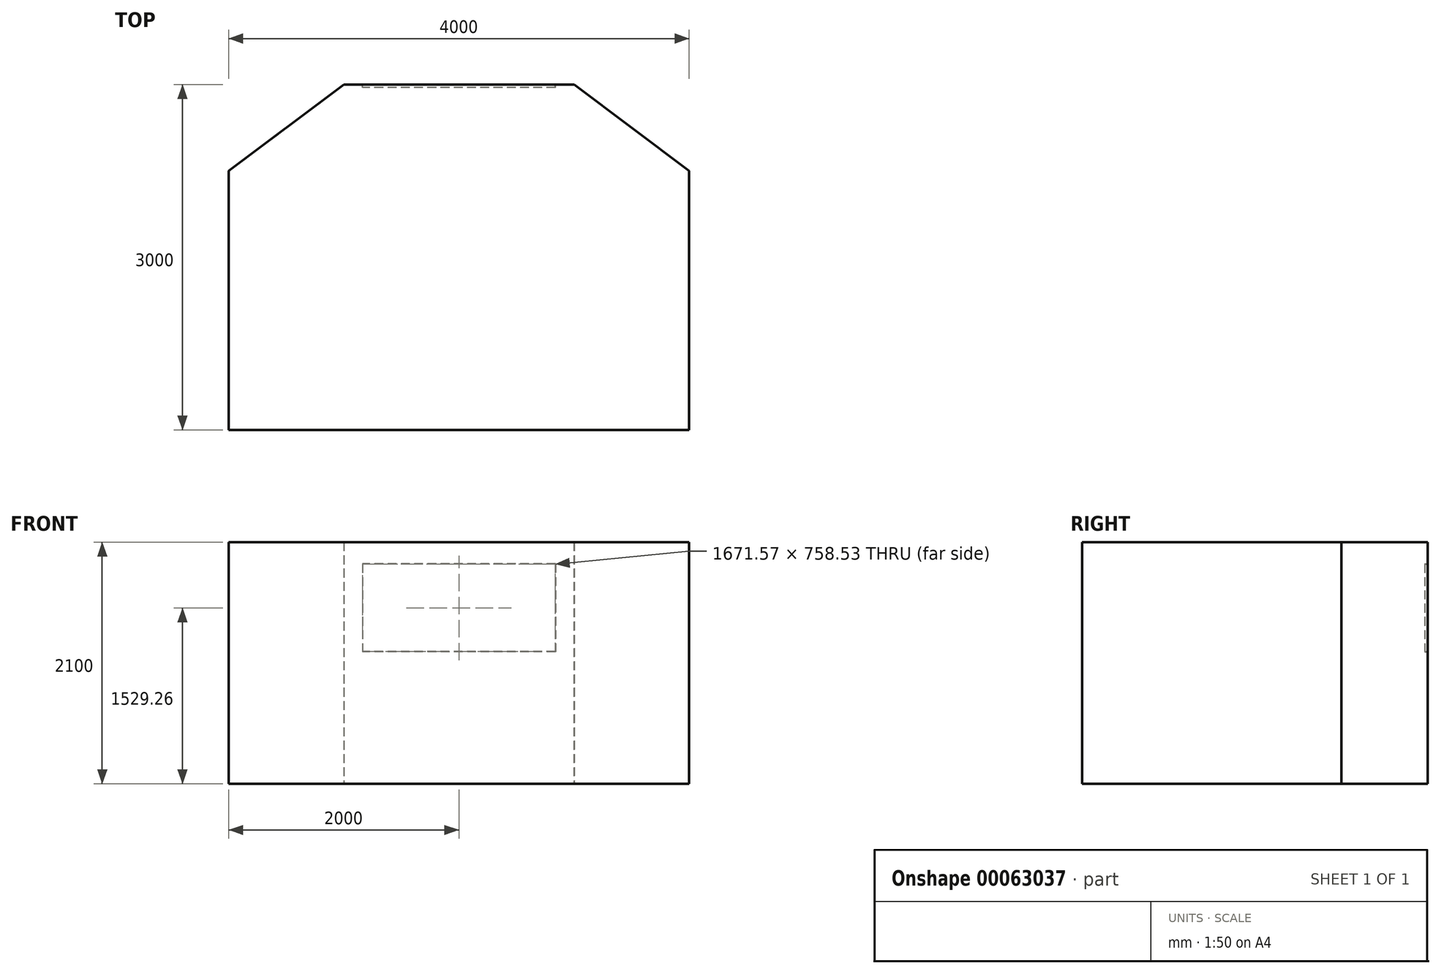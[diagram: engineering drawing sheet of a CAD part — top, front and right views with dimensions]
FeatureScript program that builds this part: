
annotation { "Feature Type Name" : "Feature", "Feature Type Description" : "" }
export const myFeature = defineFeature(function(context is Context, id is Id, definition is map)
    precondition{}
    {
        {
            var Q0;
            Q0=qCreatedBy(makeId("Top.planeOp"),FACE);
            var sketch = newSketch(context, id + "F0", { "sketchPlane" : qUnion([Q0])});
            skLineSegment(sketch, "E0.rect.bottom", {"start": v(-1000, 1500) * mm, "end": v(1000, 1500) * mm});
            skLineSegment(sketch, "E0.rect.top", {"start": v(-2000, -1500) * mm, "end": v(2000, -1500) * mm});
            skLineSegment(sketch, "E0.rect.left", {"start": v(-2000, 750) * mm, "end": v(-2000, -1500) * mm});
            skLineSegment(sketch, "E0.rect.right", {"start": v(2000, 750) * mm, "end": v(2000, -1500) * mm});
            skPoint(sketch, "E0.rect.middle", {"position": v(0, 0) * mm});
            skLineSegment(sketch, "E1", {"start": v(0, 2373.92) * mm, "end": v(0, -2394.44) * mm, "construction": true});
            skPoint(sketch, "E1.startSnap0", {"position": v(0, 1500) * mm});
            skLineSegment(sketch, "E2", {"start": v(-2000, 750) * mm, "end": v(-1000, 1500) * mm});
            skLineSegment(sketch, "E3.MirrorCS", {"start": v(2000, 750) * mm, "end": v(1000, 1500) * mm});
            skPoint(sketch, "E4.orphan", {"position": v(2000, 1500) * mm});
            skPoint(sketch, "E5.orphan", {"position": v(-2000, 1500) * mm});
            skLineSegment(sketch, "E6", {"start": v(-2000, 750) * mm, "end": v(2000, 750) * mm});
            skLineSegment(sketch, "E7", {"start": v(-2000, 0) * mm, "end": v(-500, 0) * mm});
            skLineSegment(sketch, "E8", {"start": v(-500, 0) * mm, "end": v(-500, -1500) * mm});
            skSolve(sketch);
        }
        {
            var Q0;
            {var subQ4=sQuery(id+"F0.wireOp",EDGE,"E7");Q0=makeQuery(id+"F0.imprint","IMPRINT",FACE,{"disambiguationData":[TD([[makeQuery(id+"F0.imprint","IMPRINT",EDGE,{"derivedFrom":subQ4}),-1.0]])]});}
            var Q1;
            {var subQ1=sQuery(id+"F0.wireOp",EDGE,"E0.rect.right");Q1=makeQuery(id+"F0.imprint","IMPRINT",FACE,{"disambiguationData":[TD([[makeQuery(id+"F0.imprint","IMPRINT",EDGE,{"derivedFrom":subQ1}),-1.0]])]});}
            var Q2;
            Q2=makeQuery(id+"F0.imprint","IMPRINT",FACE,{"disambiguationData":[TD([[makeQuery(id+"F0.imprint","IMPRINT",EDGE,{"derivedFrom":sQuery(id+"F0.wireOp",EDGE,"E0.rect.bottom")}),-1.0]])]});
            extrude(context, id + "F1", {"entities" : qUnion([Q0, Q1, Q2]), "depth" : 2100 * mm});
        }
        {
            var Q0;
            Q0=makeQuery(id+"F1.opExtrude","SWEPT_FACE",FACE,{"disambiguationData":[OSD([sQuery(id+"F0.wireOp",EDGE,"E0.rect.bottom")])]});
            var sketch = newSketch(context, id + "F2", { "sketchPlane" : qUnion([Q0])});
            skLineSegment(sketch, "E9.rect.bottom", {"start": v(-835.79, 1908.53) * mm, "end": v(835.79, 1908.53) * mm});
            skLineSegment(sketch, "E9.rect.top", {"start": v(-835.79, 1150) * mm, "end": v(835.79, 1150) * mm});
            skLineSegment(sketch, "E9.rect.left", {"start": v(-835.79, 1908.53) * mm, "end": v(-835.79, 1150) * mm});
            skLineSegment(sketch, "E9.rect.right", {"start": v(835.79, 1908.53) * mm, "end": v(835.79, 1150) * mm});
            skPoint(sketch, "E9.rect.middle", {"position": v(0, 1529.26) * mm});
            skLineSegment(sketch, "E10", {"start": v(0, 0) * mm, "end": v(0, 1100) * mm});
            skPoint(sketch, "E10.endSnap0", {"position": v(0, 0) * mm});
            skLineSegment(sketch, "E11", {"start": v(0, 2100) * mm, "end": v(0, 2000) * mm});
            skPoint(sketch, "E11.endSnap0", {"position": v(0, 2100) * mm});
            skSolve(sketch);
        }
        {
            var Q0;
            Q0=makeQuery(id+"F2.imprint","IMPRINT",FACE,{"disambiguationData":[TD([[makeQuery(id+"F2.imprint","IMPRINT",EDGE,{"derivedFrom":sQuery(id+"F2.wireOp",EDGE,"E9.rect.bottom")}),-1.0]])]});
            extrude(context, id + "F3", {"entities" : qUnion([Q0]), "operationType" : NewBodyOperationType.REMOVE, "oppositeDirection" : true, "depth" : 25 * mm});
        }
        {
            var Q0;
            Q0=makeQuery(id+"F3.boolean.opBoolean","COPY",FACE,{"derivedFrom":makeQuery(id+"F3.opExtrude","CAP_FACE",FACE,{"disambiguationData":[OSD([sQuery(id+"F2.wireOp",EDGE,"E9.rect.bottom"),sQuery(id+"F2.wireOp",EDGE,"E9.rect.top"),sQuery(id+"F2.wireOp",EDGE,"E9.rect.left"),sQuery(id+"F2.wireOp",EDGE,"E9.rect.right")])],"isStart":false})});
            shell(context, id + "F4", {"entities" : qUnion([Q0]), "thickness" : 2.5 * mm});
        }
    });
